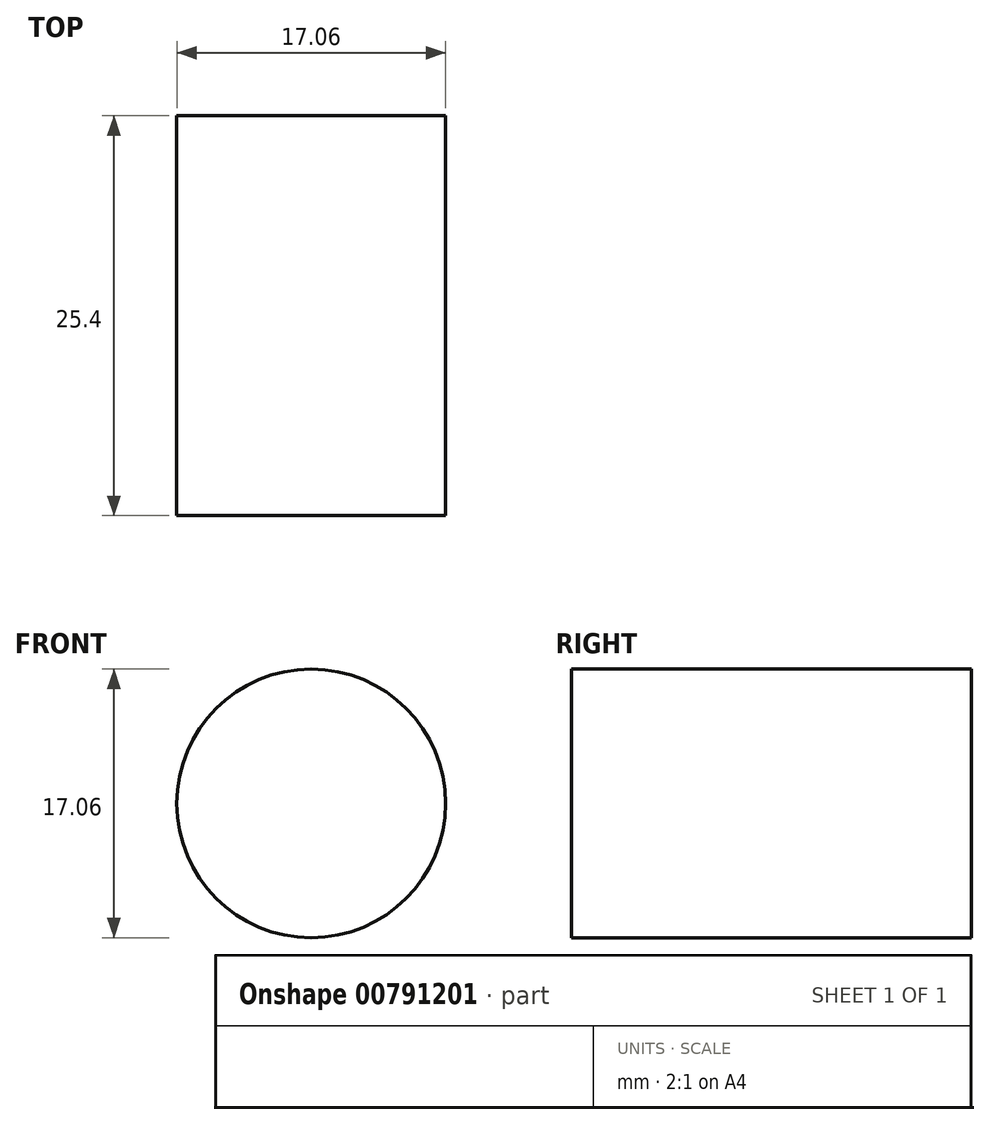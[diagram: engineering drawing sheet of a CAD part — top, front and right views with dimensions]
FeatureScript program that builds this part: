
annotation { "Feature Type Name" : "Feature", "Feature Type Description" : "" }
export const myFeature = defineFeature(function(context is Context, id is Id, definition is map)
    precondition{}
    {
        {
            var Q0;
            Q0=qCreatedBy(makeId("Front.planeOp"),FACE);
            var sketch = newSketch(context, id + "F0", { "sketchPlane" : qUnion([Q0])});
            skCircle(sketch, "E0", {"center": v(0, 0) * mm, "radius": 8.53 * mm});
            skSolve(sketch);
        }
        {
            var Q0;
            Q0=makeQuery(id+"F0.imprint","IMPRINT",FACE,{"disambiguationData":[TD([[makeQuery(id+"F0.imprint","IMPRINT",EDGE,{"derivedFrom":sQuery(id+"F0.wireOp",EDGE,"E0")}),1.0]])]});
            extrude(context, id + "F1", {"entities" : qUnion([Q0]), "depth" : 25.4 * mm, "offsetDistance" : 25.4 * mm});
        }
    });
